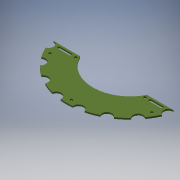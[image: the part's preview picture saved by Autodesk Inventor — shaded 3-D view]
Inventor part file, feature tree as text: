
AUTODESK INVENTOR PART (.ipt)
format: ipt  version: 2016 (Build 200138000, 138)  size: 186,880 bytes
history: native  units: mm
features: extrude x4, sketch x4, mirror x1, reference x1
ambient origin geometry x8: Origin, YZ Plane, XZ Plane, XY Plane, X Axis, Y Axis, Z Axis, Center Point
bodies: Solid1 (feature_tree)
feature tree (10):
  extrude  "Extrusion1"  TaperAngle=0.0deg  [1 undecoded]
  extrude  "Extrusion2"  TaperAngle=0.0deg  [1 undecoded]
  extrude  "Extrusion3"  Depth=1.75mm
  mirror  "Mirror1"
  extrude  "Extrusion4"  Depth=1.75mm
  sketch  "Sketch1"  dims[d0=1.75mm d1=0.0mm]
  reference  "Reference1"
  sketch  "Sketch2"  dims[d2=1.75mm d3=0.0mm]
  sketch  "Sketch3"  dims[d4=3.0mm d5=1.75mm]
  sketch  "Sketch4"  dims[d6=0.0mm d7=2.0mm d8=5.0mm d9=2.0mm d10=1.75mm d11=0.0mm]
note: 2 required parameter values undecoded (feature->parameter linkage not recoverable at this tier; creation-order binding heuristic only, values carry confidence <= 0.55)
